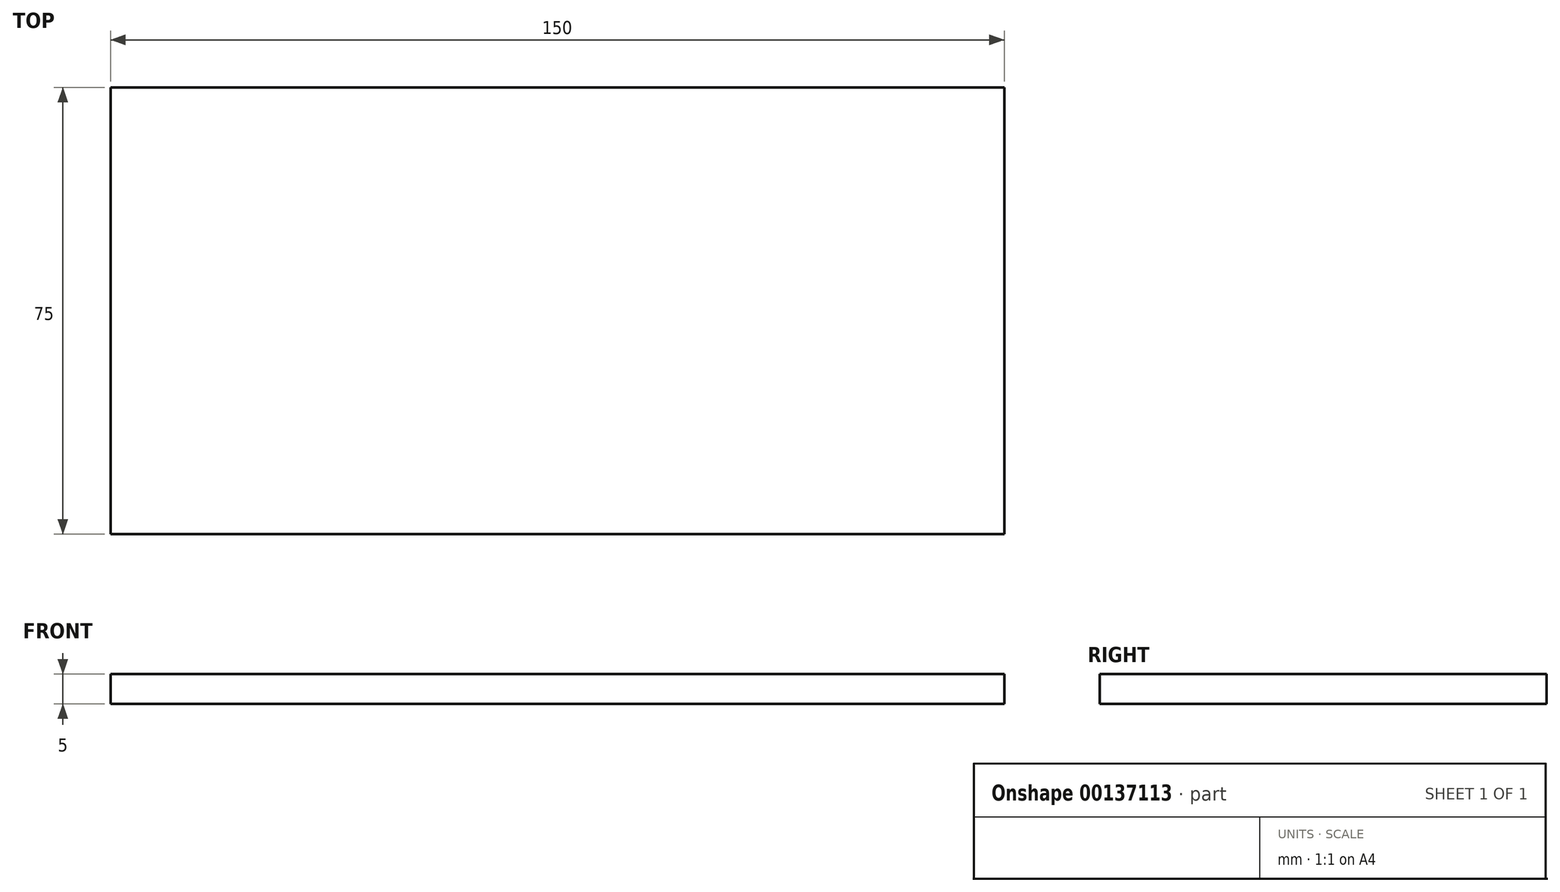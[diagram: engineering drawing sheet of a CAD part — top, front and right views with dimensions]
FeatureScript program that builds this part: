
annotation { "Feature Type Name" : "Feature", "Feature Type Description" : "" }
export const myFeature = defineFeature(function(context is Context, id is Id, definition is map)
    precondition{}
    {
        {
            var Q0;
            Q0=qCreatedBy(makeId("Top.planeOp"),FACE);
            var sketch = newSketch(context, id + "F0", { "sketchPlane" : qUnion([Q0])});
            skLineSegment(sketch, "E0.bottom", {"start": v(-75.16, 68.6) * mm, "end": v(74.84, 68.6) * mm});
            skLineSegment(sketch, "E0.top", {"start": v(-75.16, -6.4) * mm, "end": v(74.84, -6.4) * mm});
            skLineSegment(sketch, "E0.left", {"start": v(-75.16, 68.6) * mm, "end": v(-75.16, -6.4) * mm});
            skLineSegment(sketch, "E0.right", {"start": v(74.84, 68.6) * mm, "end": v(74.84, -6.4) * mm});
            skSolve(sketch);
        }
        {
            var Q0;
            Q0=makeQuery(id+"F0.imprint","IMPRINT",FACE,{"disambiguationData":[TD([[makeQuery(id+"F0.imprint","IMPRINT",EDGE,{"derivedFrom":sQuery(id+"F0.wireOp",EDGE,"E0.bottom")}),-1.0]])]});
            extrude(context, id + "F1", {"entities" : qUnion([Q0]), "depth" : 5 * mm});
        }
    });
